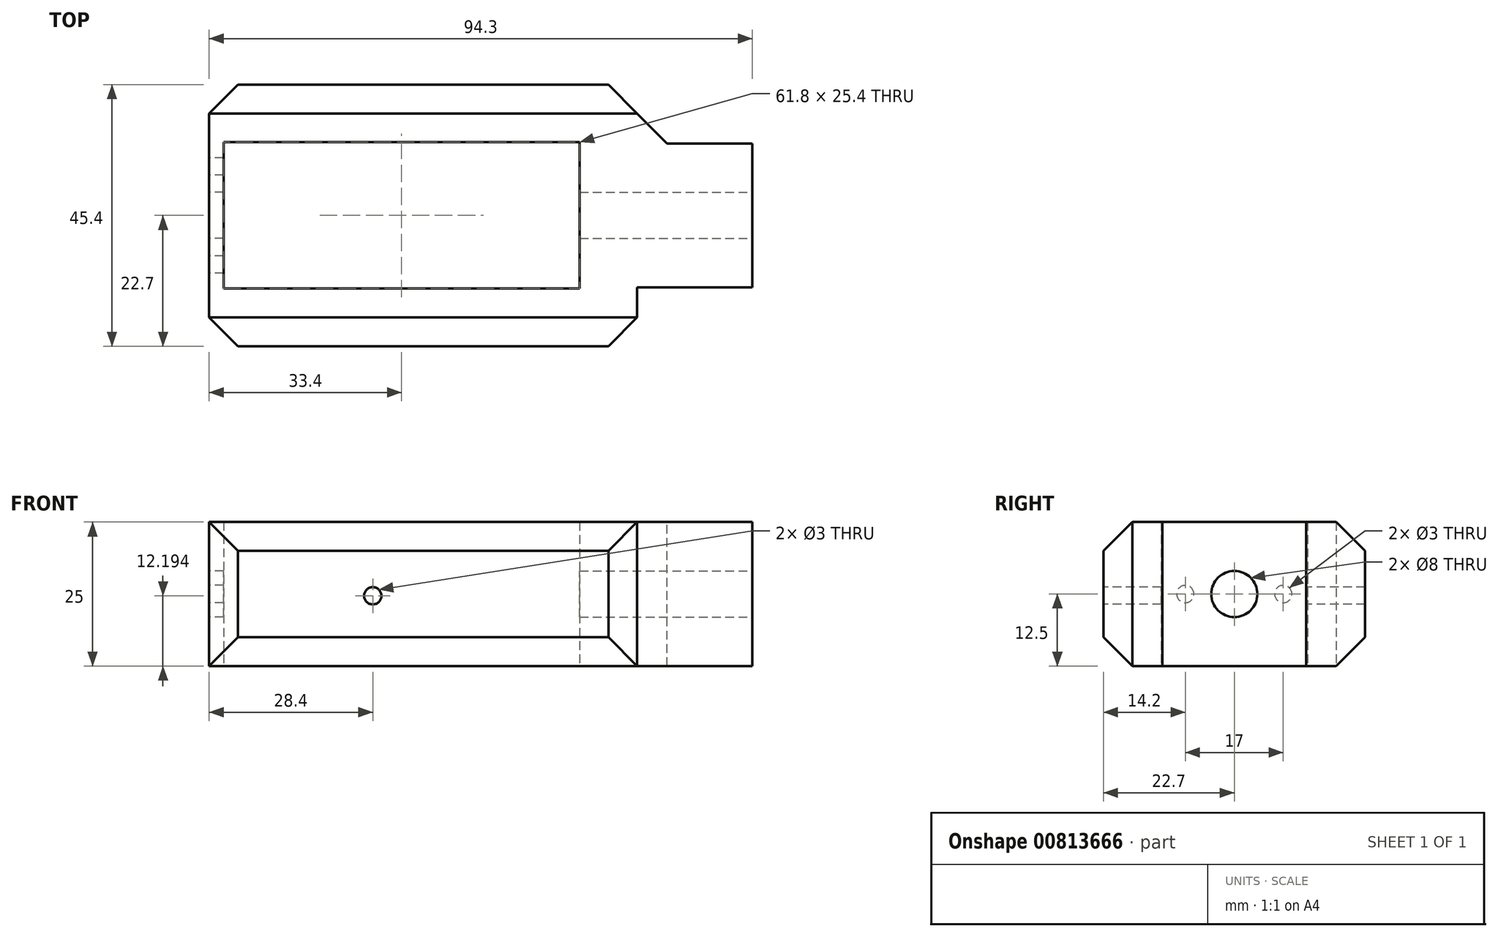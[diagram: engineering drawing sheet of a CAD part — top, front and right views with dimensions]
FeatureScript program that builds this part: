
annotation { "Feature Type Name" : "Feature", "Feature Type Description" : "" }
export const myFeature = defineFeature(function(context is Context, id is Id, definition is map)
    precondition{}
    {
        {
            var Q0;
            Q0=qCreatedBy(makeId("Top.planeOp"),FACE);
            var sketch = newSketch(context, id + "F0", { "sketchPlane" : qUnion([Q0])});
            skLineSegment(sketch, "E0.bottom", {"start": v(25.9, 12.2) * mm, "end": v(-25.9, 12.2) * mm});
            skLineSegment(sketch, "E0.top", {"start": v(25.9, -12.2) * mm, "end": v(-25.9, -12.2) * mm});
            skLineSegment(sketch, "E0.left", {"start": v(25.9, 12.2) * mm, "end": v(25.9, -12.2) * mm});
            skLineSegment(sketch, "E0.right", {"start": v(-25.9, 12.2) * mm, "end": v(-25.9, -12.2) * mm});
            skPoint(sketch, "E0.middle", {"position": v(0, 0) * mm});
            skLineSegment(sketch, "E1", {"start": v(-25.9, 12.2) * mm, "end": v(-28.4, 12.2) * mm});
            skLineSegment(sketch, "E2", {"start": v(-28.4, 12.2) * mm, "end": v(-28.4, -12.2) * mm});
            skLineSegment(sketch, "E3", {"start": v(-28.4, -12.2) * mm, "end": v(-25.9, -12.2) * mm});
            skLineSegment(sketch, "E4", {"start": v(-25.9, 12.2) * mm, "end": v(-25.9, 12.7) * mm});
            skLineSegment(sketch, "E5", {"start": v(-25.9, 12.7) * mm, "end": v(35.9, 12.7) * mm});
            skLineSegment(sketch, "E6", {"start": v(35.9, 12.7) * mm, "end": v(35.9, -12.7) * mm});
            skLineSegment(sketch, "E7", {"start": v(35.9, -12.7) * mm, "end": v(-25.9, -12.7) * mm});
            skLineSegment(sketch, "E8", {"start": v(-25.9, -12.7) * mm, "end": v(-25.9, -12.2) * mm});
            skLineSegment(sketch, "E9", {"start": v(-28.4, 12.2) * mm, "end": v(-28.4, 22.7) * mm});
            skLineSegment(sketch, "E10", {"start": v(-28.4, 22.7) * mm, "end": v(45.9, 22.7) * mm});
            skLineSegment(sketch, "E11", {"start": v(45.9, 22.7) * mm, "end": v(45.9, -22.7) * mm});
            skLineSegment(sketch, "E12", {"start": v(45.9, -22.7) * mm, "end": v(-28.4, -22.7) * mm});
            skLineSegment(sketch, "E13", {"start": v(-28.4, -22.7) * mm, "end": v(-28.4, -12.2) * mm});
            skSolve(sketch);
        }
        {
            var Q0;
            Q0=makeQuery(id+"F0.imprint","IMPRINT",FACE,{"disambiguationData":[TD([[makeQuery(id+"F0.imprint","IMPRINT",EDGE,{"derivedFrom":sQuery(id+"F0.wireOp",EDGE,"E1")}),-1.0]])]});
            var Q1;
            Q1=makeQuery(id+"F0.imprint","IMPRINT",FACE,{"disambiguationData":[TD([[makeQuery(id+"F0.imprint","IMPRINT",EDGE,{"derivedFrom":sQuery(id+"F0.wireOp",EDGE,"E0.right")}),-1.0]])]});
            extrude(context, id + "F1", {"entities" : qUnion([Q0, Q1]), "depth" : 25 * mm, "offsetDistance" : 25 * mm});
        }
        {
            var Q0;
            Q0=qCreatedBy(makeId("Right.planeOp"),FACE);
            var sketch = newSketch(context, id + "F2", { "sketchPlane" : qUnion([Q0])});
            skLineSegment(sketch, "E14", {"start": v(0, 0) * mm, "end": v(0, 12.5) * mm});
            skCircle(sketch, "E15", {"center": v(0, 12.5) * mm, "radius": 4 * mm});
            skCircle(sketch, "E16", {"center": v(-8.5, 12.5) * mm, "radius": 1.5 * mm});
            skCircle(sketch, "E17", {"center": v(8.5, 12.5) * mm, "radius": 1.5 * mm});
            skSolve(sketch);
        }
        {
            var Q0;
            Q0=qCreatedBy(makeId("Right.planeOp"),FACE);
            cPlane(context, id + "F3", {"entities" : qUnion([Q0]), "cplaneType" : CPlaneType.OFFSET, "offset" : 28.4 * mm, "oppositeDirection" : true, "width" : 150 * mm, "height" : 150 * mm});
        }
        {
            var Q0;
            Q0=qCreatedBy(id+"F3.planeOp",FACE);
            var sketch = newSketch(context, id + "F4", { "sketchPlane" : qUnion([Q0])});
            skCircle(sketch, "E18.0", {"center": v(0, 12.5) * mm, "radius": 4 * mm});
            skCircle(sketch, "E19.0", {"center": v(8.5, 12.5) * mm, "radius": 1.5 * mm});
            skCircle(sketch, "E20.0", {"center": v(-8.5, 12.5) * mm, "radius": 1.5 * mm});
            skSolve(sketch);
        }
        {
            var Q0;
            Q0=makeQuery(id+"F4.imprint","IMPRINT",FACE,{"disambiguationData":[TD([[makeQuery(id+"F4.imprint","IMPRINT",EDGE,{"derivedFrom":sQuery(id+"F4.wireOp",EDGE,"E20.0")}),1.0]])]});
            var Q1;
            Q1=makeQuery(id+"F4.imprint","IMPRINT",FACE,{"disambiguationData":[TD([[makeQuery(id+"F4.imprint","IMPRINT",EDGE,{"derivedFrom":sQuery(id+"F4.wireOp",EDGE,"E18.0")}),1.0]])]});
            var Q2;
            Q2=makeQuery(id+"F4.imprint","IMPRINT",FACE,{"disambiguationData":[TD([[makeQuery(id+"F4.imprint","IMPRINT",EDGE,{"derivedFrom":sQuery(id+"F4.wireOp",EDGE,"E19.0")}),1.0]])]});
            extrude(context, id + "F5", {"entities" : qUnion([Q0, Q1, Q2]), "operationType" : NewBodyOperationType.REMOVE, "depth" : 2.5 * mm, "offsetDistance" : 25 * mm});
        }
        {
            var Q0;
            Q0=makeQuery(id+"F1.opExtrude","SWEPT_FACE",FACE,{"disambiguationData":[OSD([sQuery(id+"F0.wireOp",EDGE,"E10")])]});
            var Q1;
            Q1=makeQuery(id+"F1.opExtrude","SWEPT_FACE",FACE,{"disambiguationData":[OSD([sQuery(id+"F0.wireOp",EDGE,"E12")])]});
            chamfer(context, id + "F6", {"entities" : qUnion([Q0, Q1]), "width" : 5 * mm, "tangentPropagation" : true});
        }
        {
            var Q0;
            Q0=qCreatedBy(makeId("Right.planeOp"),FACE);
            cPlane(context, id + "F7", {"entities" : qUnion([Q0]), "cplaneType" : CPlaneType.OFFSET, "offset" : 45.9 * mm, "width" : 150 * mm, "height" : 150 * mm});
        }
        {
            var Q0;
            Q0=qCreatedBy(id+"F7.planeOp",FACE);
            var sketch = newSketch(context, id + "F8", { "sketchPlane" : qUnion([Q0])});
            skLineSegment(sketch, "E21.bottom", {"start": v(-12.5, 25) * mm, "end": v(12.5, 25) * mm});
            skLineSegment(sketch, "E21.top", {"start": v(-12.5, 0) * mm, "end": v(12.5, 0) * mm});
            skLineSegment(sketch, "E21.left", {"start": v(-12.5, 25) * mm, "end": v(-12.5, 0) * mm});
            skLineSegment(sketch, "E21.right", {"start": v(12.5, 25) * mm, "end": v(12.5, 0) * mm});
            skPoint(sketch, "E21.middle", {"position": v(0, 12.5) * mm});
            skSolve(sketch);
        }
        {
            var Q0;
            Q0=qCreatedBy(makeId("Front.planeOp"),FACE);
            cPlane(context, id + "F9", {"entities" : qUnion([Q0]), "cplaneType" : CPlaneType.OFFSET, "offset" : 22.7 * mm, "width" : 150 * mm, "height" : 150 * mm});
        }
        {
            var Q0;
            Q0=qCreatedBy(id+"F9.planeOp",FACE);
            var sketch = newSketch(context, id + "F10", { "sketchPlane" : qUnion([Q0])});
            skCircle(sketch, "E22", {"center": v(0, 12.2) * mm, "radius": 1.5 * mm});
            skSolve(sketch);
        }
        {
            var Q0;
            Q0=makeQuery(id+"F10.imprint","IMPRINT",FACE,{"disambiguationData":[TD([[makeQuery(id+"F10.imprint","IMPRINT",EDGE,{"derivedFrom":sQuery(id+"F10.wireOp",EDGE,"E22")}),1.0]])]});
            extrude(context, id + "F11", {"entities" : qUnion([Q0]), "operationType" : NewBodyOperationType.REMOVE, "oppositeDirection" : true, "depth" : 60 * mm, "offsetDistance" : 25 * mm});
        }
        {
            var Q0;
            Q0=makeQuery(id+"F8.imprint","IMPRINT",FACE,{"disambiguationData":[TD([[makeQuery(id+"F8.imprint","IMPRINT",EDGE,{"derivedFrom":sQuery(id+"F8.wireOp",EDGE,"E21.bottom")}),-1.0]])]});
            extrude(context, id + "F12", {"entities" : qUnion([Q0]), "operationType" : NewBodyOperationType.ADD, "depth" : 20 * mm, "offsetDistance" : 25 * mm});
        }
        {
            var Q0;
            Q0=makeQuery(id+"F12.opExtrude","CAP_EDGE",EDGE,{"disambiguationData":[OSD([sQuery(id+"F8.wireOp",EDGE,"E21.right")])],"isStart":true});
            var Q1;
            Q1=makeQuery(id+"F12.opExtrude","CAP_EDGE",EDGE,{"disambiguationData":[OSD([sQuery(id+"F8.wireOp",EDGE,"E21.left")])],"isStart":true});
            chamfer(context, id + "F13", {"entities" : qUnion([Q0, Q1]), "width" : 5.2 * mm, "tangentPropagation" : true});
        }
        {
            var Q0;
            Q0=makeQuery(id+"F12.opExtrude","CAP_FACE",FACE,{"disambiguationData":[OSD([sQuery(id+"F8.wireOp",EDGE,"E21.bottom"),sQuery(id+"F8.wireOp",EDGE,"E21.top"),sQuery(id+"F8.wireOp",EDGE,"E21.left"),sQuery(id+"F8.wireOp",EDGE,"E21.right")])],"isStart":false});
            cPlane(context, id + "F14", {"entities" : qUnion([Q0]), "cplaneType" : CPlaneType.OFFSET, "offset" : 0 * mm, "width" : 150 * mm, "height" : 150 * mm});
        }
        {
            var Q0;
            Q0=qCreatedBy(id+"F14.planeOp",FACE);
            var sketch = newSketch(context, id + "F15", { "sketchPlane" : qUnion([Q0])});
            skCircle(sketch, "E23", {"center": v(0, 12.5) * mm, "radius": 4 * mm});
            skSolve(sketch);
        }
        {
            var Q0;
            Q0=makeQuery(id+"F15.imprint","IMPRINT",FACE,{"disambiguationData":[TD([[makeQuery(id+"F15.imprint","IMPRINT",EDGE,{"derivedFrom":sQuery(id+"F15.wireOp",EDGE,"E23")}),1.0]])]});
            extrude(context, id + "F16", {"entities" : qUnion([Q0]), "operationType" : NewBodyOperationType.REMOVE, "oppositeDirection" : true, "depth" : 40 * mm, "offsetDistance" : 25 * mm});
        }
    });
